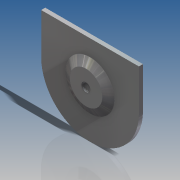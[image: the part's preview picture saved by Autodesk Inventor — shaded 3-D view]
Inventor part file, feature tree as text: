
AUTODESK INVENTOR PART (.ipt)
format: ipt  version: 2016 SP2 (Build 200236200, 236)  size: 147,968 bytes
history: native  units: in
note: dims shown in document units (in); Inventor stores cm internally (conversion verified against a paired STEP export)
features: sketch x2, extrude x1, revolve x1, fillet x1
ambient origin geometry x8: Origin, YZ Plane, XZ Plane, XY Plane, X Axis, Y Axis, Z Axis, Center Point
bodies: Solid1 (feature_tree)
feature tree (5):
  extrude  "Extrusion1"  Depth=0.3465in
  revolve  "Revolution1"  [1 undecoded]
  fillet  "Fillet1"  Radius=0.0079in
  sketch  "Sketch2"  dims[d0=0.378in d1=0.3465in]
  sketch  "Sketch3"  dims[d2=0.0157in d3=0.0in d4=0.0315in d5=0.0079in d6=0.0157in d7=0.126in d8=0.189in d9=90.0deg d10=0.0039in]
note: 1 required parameter value undecoded (feature->parameter linkage not recoverable at this tier; creation-order binding heuristic only, values carry confidence <= 0.55)
